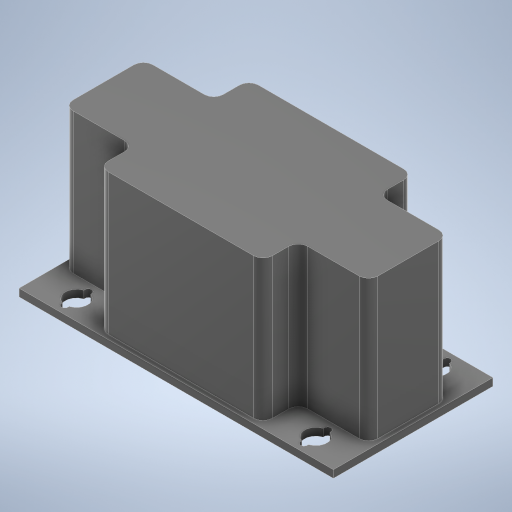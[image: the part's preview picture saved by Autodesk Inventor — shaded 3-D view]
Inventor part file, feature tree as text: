
AUTODESK INVENTOR PART (.ipt)
format: ipt  version: 2024.2 (Build 282272000, 272)  size: 314,880 bytes
history: native  units: mm
features: extrude x2, sketch x1, fillet x1
ambient origin geometry x8: Origin, YZ Plane, XZ Plane, XY Plane, X Axis, Y Axis, Z Axis, Center Point
bodies: Solid1 (feature_tree)
feature tree (4):
  sketch  "Sketch1"  dims[d0=34.0mm d1=67.0mm d7=1.6mm d8=0.0mm d9=31.6mm d10=0.0mm d18=2.0mm d19=4.8mm d33=51.0mm d34=25.5mm d38=1.0mm d43=1.0mm d44=1.0mm d46=6.5mm d47=1.5mm d48=1.0mm d50=16.0mm]
  extrude  "Extrusion1"  Depth=67.0mm
  extrude  "Extrusion2"  Depth=1.6mm TaperAngle=0.0deg
  fillet  "Fillet1"  Radius=31.6mm
